FCSTD DOCUMENT  (FreeCAD 0.19R24276 (Git))
Label: Assambly_1
License: All rights reserved
LicenseURL: http://en.wikipedia.org/wiki/All_rights_reserved
objects: Sketcher::SketchObject×1, PartDesign::Body×1
note: 2 computed .brp shape members not serialized (recipe doc carries the construction recipe); baked Part::Feature solids carry a one-line shape summary decoded from their .brp

FEATURE [Sketcher::SketchObject] Sketch  label="Master_sketch_M"
  FullyConstrained = false
  MapMode = 5
  Support = -> [XY_Plane]
  sketch-geometry (5):
    g0: LineSegment StartX=42.7681 StartY=25.9016 StartZ=0 EndX=0 EndY=-3.6e-15 EndZ=0
    g1: LineSegment StartX=0 StartY=-3.6e-15 StartZ=0 EndX=-58.6988 EndY=243.011 EndZ=0
    g2: LineSegment StartX=42.7681 StartY=25.9016 StartZ=0 EndX=-15.9307 EndY=268.913 EndZ=0
    g3: LineSegment StartX=-58.6988 StartY=243.011 StartZ=0 EndX=-15.9307 EndY=268.913 EndZ=0
    g4: LineSegment StartX=-15.9307 StartY=268.913 StartZ=0 EndX=-272.539 EndY=113.503 EndZ=0
  constraints (12):
    c: Coincident(g1,g0)
    c: Parallel(g1,g2)
    c: Equal(g1,g2)
    c: Coincident(g3,g1)
    c: Coincident(g3,g2)
    c: Coincident(g4,g2)
    c: Parallel(g3,g4)
    c: Distance(g1) = 250
    c: Distance(g0) = 50
    c: Distance(g1,g4) = 250
    c: Coincident(g0,g2)
    c: Coincident(g0,g-1)
FEATURE [PartDesign::Body] Body  label="Master_sketch_M_body"
  Group = -> [Sketch]
  Origin = -> Origin
